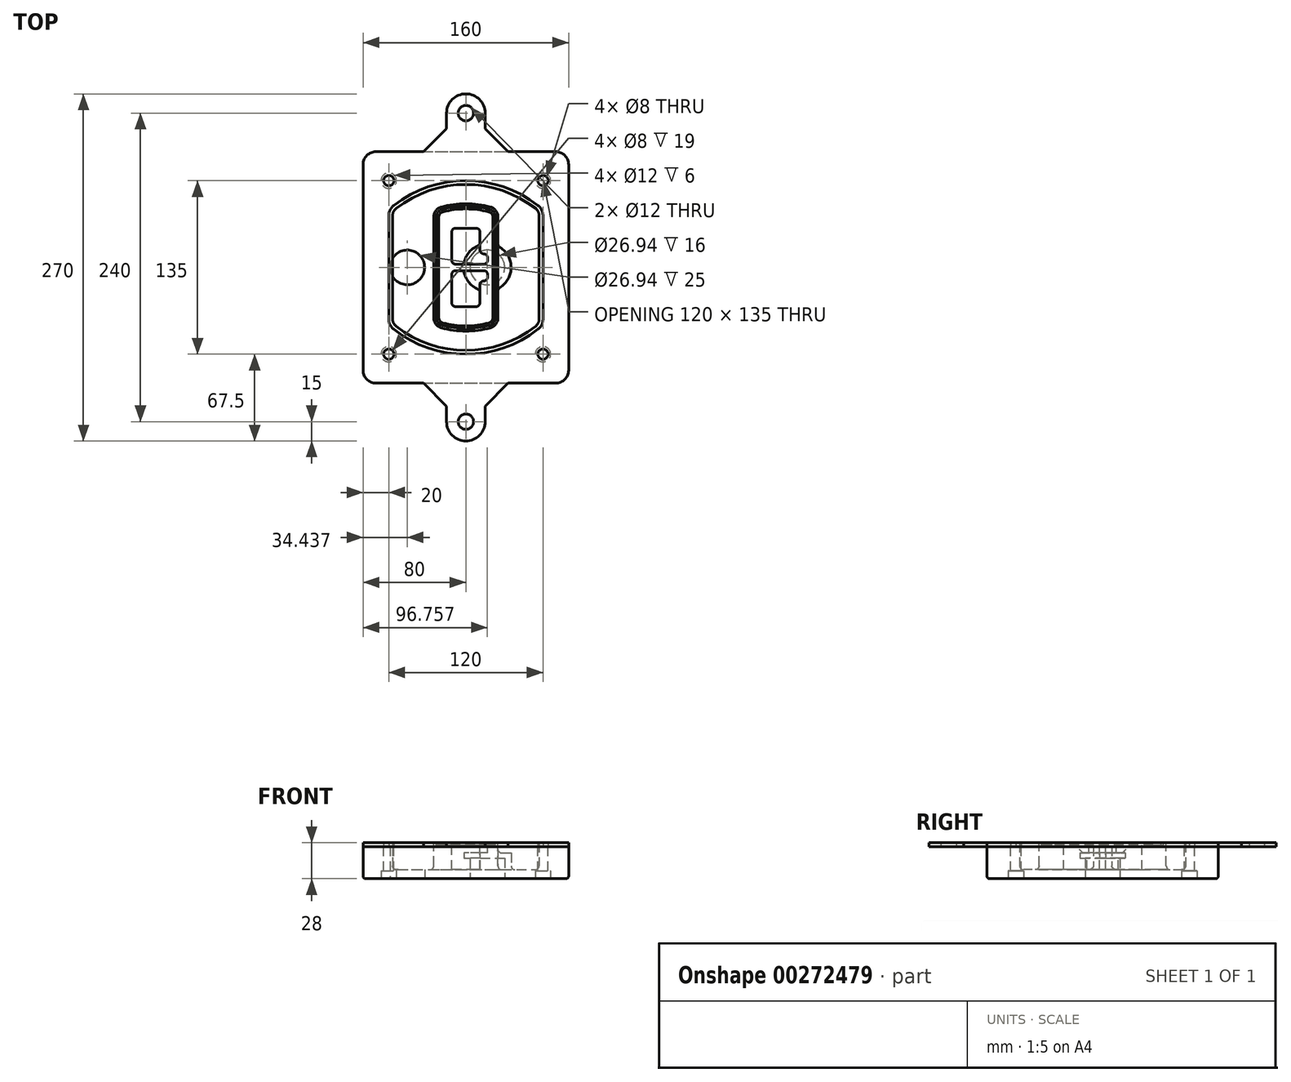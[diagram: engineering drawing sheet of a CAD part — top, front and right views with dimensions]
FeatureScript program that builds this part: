
annotation { "Feature Type Name" : "Feature", "Feature Type Description" : "" }
export const myFeature = defineFeature(function(context is Context, id is Id, definition is map)
    precondition{}
    {
        {
            var Q0;
            Q0=qCreatedBy(makeId("Top.planeOp"),FACE);
            var sketch = newSketch(context, id + "F0", { "sketchPlane" : qUnion([Q0])});
            skPoint(sketch, "E0.rect.middle", {"position": v(0, 0) * mm});
            skLineSegment(sketch, "E1.bottom", {"start": v(-70, -90) * mm, "end": v(70, -90) * mm});
            skLineSegment(sketch, "E1.top", {"start": v(-70, 90) * mm, "end": v(70, 90) * mm});
            skLineSegment(sketch, "E1.left", {"start": v(-80, -80) * mm, "end": v(-80, 80) * mm});
            skLineSegment(sketch, "E1.right", {"start": v(80, -80) * mm, "end": v(80, 80) * mm});
            skLineSegment(sketch, "E2", {"start": v(-80, 90) * mm, "end": v(80, -90) * mm, "construction": true});
            skLineSegment(sketch, "E3", {"start": v(80, 90) * mm, "end": v(-80, -90) * mm, "construction": true});
            skCircle(sketch, "E4", {"center": v(-60, 67.5) * mm, "radius": 4 * mm});
            skCircle(sketch, "E5", {"center": v(60, 67.5) * mm, "radius": 4 * mm});
            skCircle(sketch, "E6", {"center": v(60, -67.5) * mm, "radius": 4 * mm});
            skCircle(sketch, "E7", {"center": v(-60, -67.5) * mm, "radius": 4 * mm});
            skLineSegment(sketch, "E8", {"start": v(-60, 67.5) * mm, "end": v(60, 67.5) * mm, "construction": true});
            skLineSegment(sketch, "E9", {"start": v(60, 67.5) * mm, "end": v(60, -67.5) * mm, "construction": true});
            skLineSegment(sketch, "E10", {"start": v(60, -67.5) * mm, "end": v(-60, -67.5) * mm, "construction": true});
            skLineSegment(sketch, "E11", {"start": v(-60, -67.5) * mm, "end": v(-60, 67.5) * mm, "construction": true});
            skLineSegment(sketch, "E12", {"start": v(-60, 40.3) * mm, "end": v(-60, -40.3) * mm});
            skLineSegment(sketch, "E13", {"start": v(60, 40.3) * mm, "end": v(60, -40.3) * mm});
            skArc(sketch, "E14", {"start": v(56.15, 48.18) * mm, "mid": v(0, 67.5) * mm, "end": v(-56.15, 48.18) * mm});
            skArc(sketch, "E15", {"start": v(-56.15, -48.18) * mm, "mid": v(0, -67.5) * mm, "end": v(56.15, -48.18) * mm});
            skLineSegment(sketch, "E16", {"start": v(-60, 0) * mm, "end": v(60, 0) * mm, "construction": true});
            skPoint(sketch, "E17.visualSharp", {"position": v(-60, -45) * mm});
            skArc(sketch, "E17.filletArc", {"start": v(-60, -40.3) * mm, "mid": v(-58.99, -44.68) * mm, "end": v(-56.15, -48.18) * mm});
            skPoint(sketch, "E18.visualSharp", {"position": v(-60, 45) * mm});
            skArc(sketch, "E18.filletArc", {"start": v(-56.15, 48.18) * mm, "mid": v(-58.99, 44.68) * mm, "end": v(-60, 40.3) * mm});
            skPoint(sketch, "E19.visualSharp", {"position": v(60, 45) * mm});
            skArc(sketch, "E19.filletArc", {"start": v(60, 40.3) * mm, "mid": v(58.99, 44.68) * mm, "end": v(56.15, 48.18) * mm});
            skPoint(sketch, "E20.visualSharp", {"position": v(60, -45) * mm});
            skArc(sketch, "E20.filletArc", {"start": v(56.15, -48.18) * mm, "mid": v(58.99, -44.68) * mm, "end": v(60, -40.3) * mm});
            skPoint(sketch, "E21.visualSharp", {"position": v(-80, 90) * mm});
            skArc(sketch, "E21.filletArc", {"start": v(-70, 90) * mm, "mid": v(-77.07, 87.07) * mm, "end": v(-80, 80) * mm});
            skPoint(sketch, "E22.visualSharp", {"position": v(80, 90) * mm});
            skArc(sketch, "E22.filletArc", {"start": v(80, 80) * mm, "mid": v(77.07, 87.07) * mm, "end": v(70, 90) * mm});
            skPoint(sketch, "E23.visualSharp", {"position": v(80, -90) * mm});
            skArc(sketch, "E23.filletArc", {"start": v(70, -90) * mm, "mid": v(77.07, -87.07) * mm, "end": v(80, -80) * mm});
            skPoint(sketch, "E24.visualSharp", {"position": v(-80, -90) * mm});
            skArc(sketch, "E24.filletArc", {"start": v(-80, -80) * mm, "mid": v(-77.07, -87.07) * mm, "end": v(-70, -90) * mm});
            skArc(sketch, "E25.0", {"start": v(57, 40.3) * mm, "mid": v(56.3, 43.36) * mm, "end": v(54.3, 45.81) * mm});
            skLineSegment(sketch, "E25.1", {"start": v(57, 40.3) * mm, "end": v(57, -40.3) * mm});
            skArc(sketch, "E25.2", {"start": v(54.3, -45.81) * mm, "mid": v(56.3, -43.36) * mm, "end": v(57, -40.3) * mm});
            skArc(sketch, "E25.3", {"start": v(-54.3, -45.81) * mm, "mid": v(0, -64.5) * mm, "end": v(54.3, -45.81) * mm});
            skArc(sketch, "E25.4", {"start": v(-57, -40.3) * mm, "mid": v(-56.3, -43.36) * mm, "end": v(-54.3, -45.81) * mm});
            skArc(sketch, "E25.5", {"start": v(54.3, 45.81) * mm, "mid": v(0, 64.5) * mm, "end": v(-54.3, 45.81) * mm});
            skLineSegment(sketch, "E25.6", {"start": v(-57, 40.3) * mm, "end": v(-57, -40.3) * mm});
            skArc(sketch, "E25.7", {"start": v(-54.3, 45.81) * mm, "mid": v(-56.3, 43.36) * mm, "end": v(-57, 40.3) * mm});
            skArc(sketch, "E26.0", {"start": v(-58.62, 51.33) * mm, "mid": v(-62.58, 46.43) * mm, "end": v(-64, 40.3) * mm});
            skArc(sketch, "E26.1", {"start": v(58.62, 51.33) * mm, "mid": v(0, 71.5) * mm, "end": v(-58.62, 51.33) * mm});
            skArc(sketch, "E26.2", {"start": v(64, 40.3) * mm, "mid": v(62.58, 46.43) * mm, "end": v(58.62, 51.33) * mm});
            skLineSegment(sketch, "E26.3", {"start": v(64, 40.3) * mm, "end": v(64, -40.3) * mm});
            skArc(sketch, "E26.4", {"start": v(58.62, -51.33) * mm, "mid": v(62.58, -46.43) * mm, "end": v(64, -40.3) * mm});
            skLineSegment(sketch, "E26.5", {"start": v(-64, 40.3) * mm, "end": v(-64, -40.3) * mm});
            skArc(sketch, "E26.6", {"start": v(-58.62, -51.33) * mm, "mid": v(0, -71.5) * mm, "end": v(58.62, -51.33) * mm});
            skArc(sketch, "E26.7", {"start": v(-64, -40.3) * mm, "mid": v(-62.58, -46.43) * mm, "end": v(-58.62, -51.33) * mm});
            skSolve(sketch);
        }
        {
            var Q0;
            Q0=makeQuery(id+"F0.imprint","IMPRINT",FACE,{"disambiguationData":[TD([[makeQuery(id+"F0.imprint","IMPRINT",EDGE,{"derivedFrom":sQuery(id+"F0.wireOp",EDGE,"E1.bottom")}),1.0]])]});
            var Q1;
            Q1=makeQuery(id+"F0.imprint","IMPRINT",FACE,{"disambiguationData":[TD([[makeQuery(id+"F0.imprint","IMPRINT",EDGE,{"derivedFrom":sQuery(id+"F0.wireOp",EDGE,"E12")}),1.0]])]});
            var Q2;
            Q2=makeQuery(id+"F0.imprint","IMPRINT",FACE,{"disambiguationData":[TD([[makeQuery(id+"F0.imprint","IMPRINT",EDGE,{"derivedFrom":sQuery(id+"F0.wireOp",EDGE,"E25.0")}),1.0]])]});
            var Q3;
            Q3=makeQuery(id+"F0.imprint","IMPRINT",FACE,{"disambiguationData":[TD([[makeQuery(id+"F0.imprint","IMPRINT",EDGE,{"derivedFrom":sQuery(id+"F0.wireOp",EDGE,"E12")}),-1.0]])]});
            extrude(context, id + "F1", {"entities" : qUnion([Q0, Q1, Q2, Q3]), "oppositeDirection" : true, "depth" : 25 * mm});
        }
        {
            var Q0;
            Q0=makeQuery(id+"F0.imprint","IMPRINT",FACE,{"disambiguationData":[TD([[makeQuery(id+"F0.imprint","IMPRINT",EDGE,{"derivedFrom":sQuery(id+"F0.wireOp",EDGE,"E12")}),1.0]])]});
            extrude(context, id + "F2", {"entities" : qUnion([Q0]), "operationType" : NewBodyOperationType.ADD, "depth" : 3 * mm});
        }
        {
            var Q0;
            Q0=makeQuery(id+"F0.imprint","IMPRINT",FACE,{"disambiguationData":[TD([[makeQuery(id+"F0.imprint","IMPRINT",EDGE,{"derivedFrom":sQuery(id+"F0.wireOp",EDGE,"E25.0")}),1.0]])]});
            extrude(context, id + "F3", {"entities" : qUnion([Q0]), "operationType" : NewBodyOperationType.REMOVE, "oppositeDirection" : true, "depth" : 18 * mm});
        }
        {
            var Q0;
            Q0=makeQuery(id+"F2.opExtrude","CAP_FACE",FACE,{"disambiguationData":[OSD([sQuery(id+"F0.wireOp",EDGE,"E12"),sQuery(id+"F0.wireOp",EDGE,"E13"),sQuery(id+"F0.wireOp",EDGE,"E14"),sQuery(id+"F0.wireOp",EDGE,"E15"),sQuery(id+"F0.wireOp",EDGE,"E17.filletArc"),sQuery(id+"F0.wireOp",EDGE,"E18.filletArc"),sQuery(id+"F0.wireOp",EDGE,"E19.filletArc"),sQuery(id+"F0.wireOp",EDGE,"E20.filletArc"),sQuery(id+"F0.wireOp",EDGE,"E25.0"),sQuery(id+"F0.wireOp",EDGE,"E25.1"),sQuery(id+"F0.wireOp",EDGE,"E25.2"),sQuery(id+"F0.wireOp",EDGE,"E25.3"),sQuery(id+"F0.wireOp",EDGE,"E25.4"),sQuery(id+"F0.wireOp",EDGE,"E25.5"),sQuery(id+"F0.wireOp",EDGE,"E25.6"),sQuery(id+"F0.wireOp",EDGE,"E25.7")])],"isStart":false});
            var sketch = newSketch(context, id + "F4", { "sketchPlane" : qUnion([Q0])});
            skArc(sketch, "E27.0", {"start": v(-19.08, -46.97) * mm, "mid": v(0, -49.5) * mm, "end": v(19.08, -46.97) * mm});
            skArc(sketch, "E28.0", {"start": v(19.08, 46.97) * mm, "mid": v(0, 49.5) * mm, "end": v(-19.08, 46.97) * mm});
            skLineSegment(sketch, "E29", {"start": v(-25, 39.25) * mm, "end": v(-25, -39.25) * mm});
            skLineSegment(sketch, "E30", {"start": v(25, 39.25) * mm, "end": v(25, -39.25) * mm});
            skLineSegment(sketch, "E31", {"start": v(-25, 45.1) * mm, "end": v(25, 45.1) * mm, "construction": true});
            skLineSegment(sketch, "E32", {"start": v(-25, -45.1) * mm, "end": v(25, -45.1) * mm, "construction": true});
            skPoint(sketch, "E33.visualSharp", {"position": v(-25, 45.1) * mm});
            skArc(sketch, "E33.filletArc", {"start": v(-19.08, 46.97) * mm, "mid": v(-23.35, 44.11) * mm, "end": v(-25, 39.25) * mm});
            skPoint(sketch, "E34.visualSharp", {"position": v(25, 45.1) * mm});
            skArc(sketch, "E34.filletArc", {"start": v(25, 39.25) * mm, "mid": v(23.35, 44.11) * mm, "end": v(19.08, 46.97) * mm});
            skPoint(sketch, "E35.visualSharp", {"position": v(25, -45.1) * mm});
            skArc(sketch, "E35.filletArc", {"start": v(19.08, -46.97) * mm, "mid": v(23.35, -44.11) * mm, "end": v(25, -39.25) * mm});
            skPoint(sketch, "E36.visualSharp", {"position": v(-25, -45.1) * mm});
            skArc(sketch, "E36.filletArc", {"start": v(-25, -39.25) * mm, "mid": v(-23.35, -44.11) * mm, "end": v(-19.08, -46.97) * mm});
            skArc(sketch, "E37.0", {"start": v(54.3, 45.81) * mm, "mid": v(0, 64.5) * mm, "end": v(-54.3, 45.81) * mm});
            skArc(sketch, "E37.1", {"start": v(-54.3, 45.81) * mm, "mid": v(-56.3, 43.36) * mm, "end": v(-57, 40.3) * mm});
            skLineSegment(sketch, "E37.2", {"start": v(-57, 40.3) * mm, "end": v(-57, -40.3) * mm});
            skArc(sketch, "E37.3", {"start": v(-57, -40.3) * mm, "mid": v(-56.3, -43.36) * mm, "end": v(-54.3, -45.81) * mm});
            skArc(sketch, "E37.4", {"start": v(-54.3, -45.81) * mm, "mid": v(0, -64.5) * mm, "end": v(54.3, -45.81) * mm});
            skArc(sketch, "E37.5", {"start": v(54.3, -45.81) * mm, "mid": v(56.3, -43.36) * mm, "end": v(57, -40.3) * mm});
            skLineSegment(sketch, "E37.6", {"start": v(57, 40.3) * mm, "end": v(57, -40.3) * mm});
            skArc(sketch, "E37.7", {"start": v(57, 40.3) * mm, "mid": v(56.3, 43.36) * mm, "end": v(54.3, 45.81) * mm});
            skLineSegment(sketch, "E38.0", {"start": v(23, 39.25) * mm, "end": v(23, -39.25) * mm});
            skArc(sketch, "E38.1", {"start": v(18.56, -45.04) * mm, "mid": v(21.76, -42.9) * mm, "end": v(23, -39.25) * mm});
            skArc(sketch, "E38.2", {"start": v(-18.56, -45.04) * mm, "mid": v(0, -47.5) * mm, "end": v(18.56, -45.04) * mm});
            skArc(sketch, "E38.3", {"start": v(-23, -39.25) * mm, "mid": v(-21.76, -42.9) * mm, "end": v(-18.56, -45.04) * mm});
            skLineSegment(sketch, "E38.4", {"start": v(-23, 39.25) * mm, "end": v(-23, -39.25) * mm});
            skArc(sketch, "E38.5", {"start": v(23, 39.25) * mm, "mid": v(21.76, 42.9) * mm, "end": v(18.56, 45.04) * mm});
            skArc(sketch, "E38.6", {"start": v(-18.56, 45.04) * mm, "mid": v(-21.76, 42.9) * mm, "end": v(-23, 39.25) * mm});
            skArc(sketch, "E38.7", {"start": v(18.56, 45.04) * mm, "mid": v(0, 47.5) * mm, "end": v(-18.56, 45.04) * mm});
            skArc(sketch, "E39.0", {"start": v(21, 39.25) * mm, "mid": v(20.18, 41.68) * mm, "end": v(18.04, 43.1) * mm});
            skLineSegment(sketch, "E39.1", {"start": v(21, 39.25) * mm, "end": v(21, -39.25) * mm});
            skArc(sketch, "E39.2", {"start": v(18.04, -43.1) * mm, "mid": v(20.18, -41.68) * mm, "end": v(21, -39.25) * mm});
            skArc(sketch, "E39.3", {"start": v(-18.04, -43.1) * mm, "mid": v(0, -45.5) * mm, "end": v(18.04, -43.1) * mm});
            skArc(sketch, "E39.4", {"start": v(-21, -39.25) * mm, "mid": v(-20.18, -41.68) * mm, "end": v(-18.04, -43.1) * mm});
            skArc(sketch, "E39.5", {"start": v(18.04, 43.1) * mm, "mid": v(0, 45.5) * mm, "end": v(-18.04, 43.1) * mm});
            skLineSegment(sketch, "E39.6", {"start": v(-21, 39.25) * mm, "end": v(-21, -39.25) * mm});
            skArc(sketch, "E39.7", {"start": v(-18.04, 43.1) * mm, "mid": v(-20.18, 41.68) * mm, "end": v(-21, 39.25) * mm});
            skLineSegment(sketch, "E40", {"start": v(-25, 0) * mm, "end": v(25, 0) * mm, "construction": true});
            skLineSegment(sketch, "E41", {"start": v(-11, 5.5) * mm, "end": v(-11, 27.5) * mm});
            skLineSegment(sketch, "E42", {"start": v(-8, 30.5) * mm, "end": v(8, 30.5) * mm});
            skLineSegment(sketch, "E43", {"start": v(11, 27.5) * mm, "end": v(11, 13.5) * mm});
            skLineSegment(sketch, "E44", {"start": v(14, 10.5) * mm, "end": v(14, 10.5) * mm});
            skLineSegment(sketch, "E45", {"start": v(17, 7.5) * mm, "end": v(17, 5.5) * mm});
            skLineSegment(sketch, "E46", {"start": v(14, 2.5) * mm, "end": v(-8, 2.5) * mm});
            skPoint(sketch, "E47.visualSharp", {"position": v(-11, 30.5) * mm});
            skArc(sketch, "E47.filletArc", {"start": v(-8, 30.5) * mm, "mid": v(-10.12, 29.62) * mm, "end": v(-11, 27.5) * mm});
            skPoint(sketch, "E48.visualSharp", {"position": v(11, 30.5) * mm});
            skArc(sketch, "E48.filletArc", {"start": v(11, 27.5) * mm, "mid": v(10.12, 29.62) * mm, "end": v(8, 30.5) * mm});
            skPoint(sketch, "E49.visualSharp", {"position": v(11, 10.5) * mm});
            skArc(sketch, "E49.filletArc", {"start": v(11, 13.5) * mm, "mid": v(11.88, 11.38) * mm, "end": v(14, 10.5) * mm});
            skPoint(sketch, "E50.visualSharp", {"position": v(17, 10.5) * mm});
            skArc(sketch, "E50.filletArc", {"start": v(17, 7.5) * mm, "mid": v(16.12, 9.62) * mm, "end": v(14, 10.5) * mm});
            skPoint(sketch, "E51.visualSharp", {"position": v(17, 2.5) * mm});
            skArc(sketch, "E51.filletArc", {"start": v(14, 2.5) * mm, "mid": v(16.12, 3.38) * mm, "end": v(17, 5.5) * mm});
            skPoint(sketch, "E52.visualSharp", {"position": v(-11, 2.5) * mm});
            skArc(sketch, "E52.filletArc", {"start": v(-11, 5.5) * mm, "mid": v(-10.12, 3.38) * mm, "end": v(-8, 2.5) * mm});
            skLineSegment(sketch, "E53.0.MirrorCS", {"start": v(14, -2.5) * mm, "end": v(-8, -2.5) * mm});
            skArc(sketch, "E54.0.MirrorCS", {"start": v(-11, -5.5) * mm, "mid": v(-10.12, -3.38) * mm, "end": v(-8, -2.5) * mm});
            skLineSegment(sketch, "E55.0.MirrorCS", {"start": v(-11, -5.5) * mm, "end": v(-11, -27.5) * mm});
            skArc(sketch, "E56.0.MirrorCS", {"start": v(-8, -30.5) * mm, "mid": v(-10.12, -29.62) * mm, "end": v(-11, -27.5) * mm});
            skLineSegment(sketch, "E57.0.MirrorCS", {"start": v(-8, -30.5) * mm, "end": v(8, -30.5) * mm});
            skArc(sketch, "E58.0.MirrorCS", {"start": v(11, -27.5) * mm, "mid": v(10.12, -29.62) * mm, "end": v(8, -30.5) * mm});
            skLineSegment(sketch, "E59.0.MirrorCS", {"start": v(11, -27.5) * mm, "end": v(11, -13.5) * mm});
            skArc(sketch, "E60.0.MirrorCS", {"start": v(11, -13.5) * mm, "mid": v(11.88, -11.38) * mm, "end": v(14, -10.5) * mm});
            skArc(sketch, "E61.0.MirrorCS", {"start": v(17, -7.5) * mm, "mid": v(16.12, -9.62) * mm, "end": v(14, -10.5) * mm});
            skLineSegment(sketch, "E62.0.MirrorCS", {"start": v(17, -7.5) * mm, "end": v(17, -5.5) * mm});
            skArc(sketch, "E63.0.MirrorCS", {"start": v(14, -2.5) * mm, "mid": v(16.12, -3.38) * mm, "end": v(17, -5.5) * mm});
            skSolve(sketch);
        }
        {
            var Q0;
            Q0=makeQuery(id+"F4.imprint","IMPRINT",FACE,{"disambiguationData":[TD([[makeQuery(id+"F4.imprint","IMPRINT",EDGE,{"derivedFrom":sQuery(id+"F4.wireOp",EDGE,"E27.0")}),1.0]])]});
            var Q1;
            Q1=makeQuery(id+"F4.imprint","IMPRINT",FACE,{"disambiguationData":[TD([[makeQuery(id+"F4.imprint","IMPRINT",EDGE,{"derivedFrom":sQuery(id+"F4.wireOp",EDGE,"E38.0")}),-1.0]])]});
            var Q2;
            Q2=makeQuery(id+"F4.imprint","IMPRINT",FACE,{"disambiguationData":[TD([[makeQuery(id+"F4.imprint","IMPRINT",EDGE,{"derivedFrom":sQuery(id+"F4.wireOp",EDGE,"E39.0")}),1.0]])]});
            extrude(context, id + "F5", {"entities" : qUnion([Q0, Q1, Q2]), "operationType" : NewBodyOperationType.ADD, "endBound" : BoundingType.UP_TO_NEXT, "oppositeDirection" : true, "depth" : 25 * mm});
        }
        {
            var Q0;
            Q0=makeQuery(id+"F4.imprint","IMPRINT",FACE,{"disambiguationData":[TD([[makeQuery(id+"F4.imprint","IMPRINT",EDGE,{"derivedFrom":sQuery(id+"F4.wireOp",EDGE,"E38.0")}),-1.0]])]});
            extrude(context, id + "F6", {"entities" : qUnion([Q0]), "operationType" : NewBodyOperationType.REMOVE, "oppositeDirection" : true, "depth" : 2 * mm});
        }
        {
            var Q0;
            Q0=makeQuery(id+"F1.opExtrude","CAP_FACE",FACE,{"disambiguationData":[OSD([sQuery(id+"F0.wireOp",EDGE,"E1.bottom"),sQuery(id+"F0.wireOp",EDGE,"E1.top"),sQuery(id+"F0.wireOp",EDGE,"E1.left"),sQuery(id+"F0.wireOp",EDGE,"E1.right"),sQuery(id+"F0.wireOp",EDGE,"E4"),sQuery(id+"F0.wireOp",EDGE,"E5"),sQuery(id+"F0.wireOp",EDGE,"E6"),sQuery(id+"F0.wireOp",EDGE,"E7"),sQuery(id+"F0.wireOp",EDGE,"E21.filletArc"),sQuery(id+"F0.wireOp",EDGE,"E22.filletArc"),sQuery(id+"F0.wireOp",EDGE,"E23.filletArc"),sQuery(id+"F0.wireOp",EDGE,"E24.filletArc")])],"isStart":false});
            var sketch = newSketch(context, id + "F7", { "sketchPlane" : qUnion([Q0])});
            skCircle(sketch, "E64", {"center": v(16.76, 0) * mm, "radius": 13.47 * mm});
            skCircle(sketch, "E65", {"center": v(-45.56, 0) * mm, "radius": 13.47 * mm});
            skLineSegment(sketch, "E66", {"start": v(80, 0) * mm, "end": v(-80, 0) * mm});
            skCircle(sketch, "E67", {"center": v(16.76, 0) * mm, "radius": 18.47 * mm});
            skCircle(sketch, "E68", {"center": v(60, -67.5) * mm, "radius": 6 * mm});
            skCircle(sketch, "E69", {"center": v(-60, -67.5) * mm, "radius": 6 * mm});
            skCircle(sketch, "E70", {"center": v(-60, 67.5) * mm, "radius": 6 * mm});
            skCircle(sketch, "E71", {"center": v(60, 67.5) * mm, "radius": 6 * mm});
            skSolve(sketch);
        }
        {
            var Q0;
            {var subQ1=sQuery(id+"F7.wireOp",EDGE,"E66");var subQ4=sQuery(id+"F7.wireOp",EDGE,"E64");var subQ6=makeQuery(id+"F7.imprint","INTERSECT",VERTEX,{"disambiguationData":[OD(0.0)],"derivedFrom":[subQ4,subQ1]});Q0=makeQuery(id+"F7.imprint","IMPRINT",FACE,{"disambiguationData":[TD([[makeQuery(id+"F7.imprint","IMPRINT",EDGE,{"disambiguationData":[TD([[subQ6,-1.0]])],"derivedFrom":subQ4}),-1.0]])]});}
            var Q1;
            {var subQ0=sQuery(id+"F7.wireOp",EDGE,"E66");var subQ1=sQuery(id+"F7.wireOp",EDGE,"E64");var subQ3=makeQuery(id+"F7.imprint","INTERSECT",VERTEX,{"disambiguationData":[OD(0.0)],"derivedFrom":[subQ1,subQ0]});Q1=makeQuery(id+"F7.imprint","IMPRINT",FACE,{"disambiguationData":[TD([[makeQuery(id+"F7.imprint","IMPRINT",EDGE,{"disambiguationData":[TD([[subQ3,-1.0]])],"derivedFrom":subQ1}),1.0]])]});}
            var Q2;
            {var subQ0=sQuery(id+"F7.wireOp",EDGE,"E66");var subQ1=sQuery(id+"F7.wireOp",EDGE,"E64");var subQ3=makeQuery(id+"F7.imprint","INTERSECT",VERTEX,{"disambiguationData":[OD(0.0)],"derivedFrom":[subQ1,subQ0]});Q2=makeQuery(id+"F7.imprint","IMPRINT",FACE,{"disambiguationData":[TD([[makeQuery(id+"F7.imprint","IMPRINT",EDGE,{"disambiguationData":[TD([[subQ3,1.0]])],"derivedFrom":subQ1}),1.0]])]});}
            var Q3;
            {var subQ1=sQuery(id+"F7.wireOp",EDGE,"E66");var subQ4=sQuery(id+"F7.wireOp",EDGE,"E64");var subQ6=makeQuery(id+"F7.imprint","INTERSECT",VERTEX,{"disambiguationData":[OD(0.0)],"derivedFrom":[subQ4,subQ1]});Q3=makeQuery(id+"F7.imprint","IMPRINT",FACE,{"disambiguationData":[TD([[makeQuery(id+"F7.imprint","IMPRINT",EDGE,{"disambiguationData":[TD([[subQ6,1.0]])],"derivedFrom":subQ4}),-1.0]])]});}
            extrude(context, id + "F8", {"entities" : qUnion([Q0, Q1, Q2, Q3]), "operationType" : NewBodyOperationType.ADD, "oppositeDirection" : true, "depth" : 20 * mm});
        }
        {
            var Q0;
            {var subQ0=sQuery(id+"F7.wireOp",EDGE,"E66");var subQ1=sQuery(id+"F7.wireOp",EDGE,"E64");var subQ3=makeQuery(id+"F7.imprint","INTERSECT",VERTEX,{"disambiguationData":[OD(0.0)],"derivedFrom":[subQ1,subQ0]});Q0=makeQuery(id+"F7.imprint","IMPRINT",FACE,{"disambiguationData":[TD([[makeQuery(id+"F7.imprint","IMPRINT",EDGE,{"disambiguationData":[TD([[subQ3,-1.0]])],"derivedFrom":subQ1}),1.0]])]});}
            var Q1;
            {var subQ0=sQuery(id+"F7.wireOp",EDGE,"E66");var subQ1=sQuery(id+"F7.wireOp",EDGE,"E64");var subQ3=makeQuery(id+"F7.imprint","INTERSECT",VERTEX,{"disambiguationData":[OD(0.0)],"derivedFrom":[subQ1,subQ0]});Q1=makeQuery(id+"F7.imprint","IMPRINT",FACE,{"disambiguationData":[TD([[makeQuery(id+"F7.imprint","IMPRINT",EDGE,{"disambiguationData":[TD([[subQ3,1.0]])],"derivedFrom":subQ1}),1.0]])]});}
            extrude(context, id + "F9", {"entities" : qUnion([Q0, Q1]), "operationType" : NewBodyOperationType.REMOVE, "oppositeDirection" : true, "depth" : 16 * mm});
        }
        {
            var Q0;
            {var subQ0=sQuery(id+"F7.wireOp",EDGE,"E66");var subQ1=sQuery(id+"F7.wireOp",EDGE,"E65");var subQ3=makeQuery(id+"F7.imprint","INTERSECT",VERTEX,{"disambiguationData":[OD(0.0)],"derivedFrom":[subQ1,subQ0]});Q0=makeQuery(id+"F7.imprint","IMPRINT",FACE,{"disambiguationData":[TD([[makeQuery(id+"F7.imprint","IMPRINT",EDGE,{"disambiguationData":[TD([[subQ3,-1.0]])],"derivedFrom":subQ1}),1.0]])]});}
            var Q1;
            {var subQ0=sQuery(id+"F7.wireOp",EDGE,"E66");var subQ1=sQuery(id+"F7.wireOp",EDGE,"E65");var subQ3=makeQuery(id+"F7.imprint","INTERSECT",VERTEX,{"disambiguationData":[OD(0.0)],"derivedFrom":[subQ1,subQ0]});Q1=makeQuery(id+"F7.imprint","IMPRINT",FACE,{"disambiguationData":[TD([[makeQuery(id+"F7.imprint","IMPRINT",EDGE,{"disambiguationData":[TD([[subQ3,1.0]])],"derivedFrom":subQ1}),1.0]])]});}
            extrude(context, id + "F10", {"entities" : qUnion([Q0, Q1]), "operationType" : NewBodyOperationType.REMOVE, "oppositeDirection" : true, "depth" : 25 * mm});
        }
        {
            var Q0;
            Q0=makeQuery(id+"F7.imprint","IMPRINT",FACE,{"disambiguationData":[TD([[makeQuery(id+"F7.imprint","IMPRINT",EDGE,{"derivedFrom":sQuery(id+"F7.wireOp",EDGE,"E68")}),1.0]])]});
            var Q1;
            Q1=makeQuery(id+"F7.imprint","IMPRINT",FACE,{"disambiguationData":[TD([[makeQuery(id+"F7.imprint","IMPRINT",EDGE,{"derivedFrom":makeQuery(id+"F1.opExtrude","CAP_EDGE",EDGE,{"disambiguationData":[OSD([sQuery(id+"F0.wireOp",EDGE,"E5")])],"isStart":false})}),-1.0]])]});
            var Q2;
            Q2=makeQuery(id+"F7.imprint","IMPRINT",FACE,{"disambiguationData":[TD([[makeQuery(id+"F7.imprint","IMPRINT",EDGE,{"derivedFrom":sQuery(id+"F7.wireOp",EDGE,"E69")}),1.0]])]});
            var Q3;
            Q3=makeQuery(id+"F7.imprint","IMPRINT",FACE,{"disambiguationData":[TD([[makeQuery(id+"F7.imprint","IMPRINT",EDGE,{"derivedFrom":makeQuery(id+"F1.opExtrude","CAP_EDGE",EDGE,{"disambiguationData":[OSD([sQuery(id+"F0.wireOp",EDGE,"E4")])],"isStart":false})}),-1.0]])]});
            var Q4;
            Q4=makeQuery(id+"F7.imprint","IMPRINT",FACE,{"disambiguationData":[TD([[makeQuery(id+"F7.imprint","IMPRINT",EDGE,{"derivedFrom":sQuery(id+"F7.wireOp",EDGE,"E70")}),1.0]])]});
            var Q5;
            Q5=makeQuery(id+"F7.imprint","IMPRINT",FACE,{"disambiguationData":[TD([[makeQuery(id+"F7.imprint","IMPRINT",EDGE,{"derivedFrom":makeQuery(id+"F1.opExtrude","CAP_EDGE",EDGE,{"disambiguationData":[OSD([sQuery(id+"F0.wireOp",EDGE,"E7")])],"isStart":false})}),-1.0]])]});
            var Q6;
            Q6=makeQuery(id+"F7.imprint","IMPRINT",FACE,{"disambiguationData":[TD([[makeQuery(id+"F7.imprint","IMPRINT",EDGE,{"derivedFrom":sQuery(id+"F7.wireOp",EDGE,"E71")}),1.0]])]});
            var Q7;
            Q7=makeQuery(id+"F7.imprint","IMPRINT",FACE,{"disambiguationData":[TD([[makeQuery(id+"F7.imprint","IMPRINT",EDGE,{"derivedFrom":makeQuery(id+"F1.opExtrude","CAP_EDGE",EDGE,{"disambiguationData":[OSD([sQuery(id+"F0.wireOp",EDGE,"E6")])],"isStart":false})}),-1.0]])]});
            extrude(context, id + "F11", {"entities" : qUnion([Q0, Q1, Q2, Q3, Q4, Q5, Q6, Q7]), "operationType" : NewBodyOperationType.REMOVE, "oppositeDirection" : true, "depth" : 6 * mm});
        }
        {
            var Q0;
            Q0=makeQuery(id+"F9.boolean.opBoolean","COPY",FACE,{"derivedFrom":makeQuery(id+"F9.opExtrude","CAP_FACE",FACE,{"disambiguationData":[OSD([sQuery(id+"F7.wireOp",EDGE,"E64")])],"isStart":false})});
            var sketch = newSketch(context, id + "F12", { "sketchPlane" : qUnion([Q0])});
            skArc(sketch, "E72.0", {"start": v(11, 17.55) * mm, "mid": v(2.57, 11.82) * mm, "end": v(-1.54, 2.5) * mm});
            skArc(sketch, "E72.1", {"start": v(-1.54, -2.5) * mm, "mid": v(2.57, -11.82) * mm, "end": v(11, -17.55) * mm});
            skLineSegment(sketch, "E73", {"start": v(-1.54, -2.5) * mm, "end": v(14, -2.5) * mm});
            skLineSegment(sketch, "E74.0", {"start": v(14, 2.5) * mm, "end": v(-1.54, 2.5) * mm});
            skArc(sketch, "E74.1", {"start": v(14, 2.5) * mm, "mid": v(16.12, 3.38) * mm, "end": v(17, 5.5) * mm});
            skLineSegment(sketch, "E74.2", {"start": v(17, 7.5) * mm, "end": v(17, 5.5) * mm});
            skArc(sketch, "E74.3", {"start": v(17, 7.5) * mm, "mid": v(16.12, 9.62) * mm, "end": v(14, 10.5) * mm});
            skArc(sketch, "E74.4", {"start": v(11, 13.5) * mm, "mid": v(11.88, 11.38) * mm, "end": v(14, 10.5) * mm});
            skLineSegment(sketch, "E74.5", {"start": v(11, 17.55) * mm, "end": v(11, 13.5) * mm});
            skLineSegment(sketch, "E74.7", {"start": v(14, -2.5) * mm, "end": v(-1.54, -2.5) * mm});
            skArc(sketch, "E74.8", {"start": v(14, -2.5) * mm, "mid": v(16.12, -3.38) * mm, "end": v(17, -5.5) * mm});
            skLineSegment(sketch, "E74.9", {"start": v(17, -7.5) * mm, "end": v(17, -5.5) * mm});
            skArc(sketch, "E74.10", {"start": v(17, -7.5) * mm, "mid": v(16.12, -9.62) * mm, "end": v(14, -10.5) * mm});
            skArc(sketch, "E74.11", {"start": v(11, -13.5) * mm, "mid": v(11.88, -11.38) * mm, "end": v(14, -10.5) * mm});
            skLineSegment(sketch, "E74.12", {"start": v(11, -17.55) * mm, "end": v(11, -13.5) * mm});
            skPoint(sketch, "E75.orphan", {"position": v(11, -27.5) * mm});
            skPoint(sketch, "E76.orphan", {"position": v(-8, -2.5) * mm});
            skPoint(sketch, "E77.orphan", {"position": v(-8, 2.5) * mm});
            skPoint(sketch, "E78.orphan", {"position": v(11, 27.5) * mm});
            skSolve(sketch);
        }
        {
            var Q0;
            {var subQ7=sQuery(id+"F12.wireOp",EDGE,"E72.0");var subQ14=sQuery(id+"F12.wireOp",EDGE,"E72.1");var subQ16=sQuery(id+"F12.wireOp",EDGE,"E74.1");var subQ18=sQuery(id+"F12.wireOp",EDGE,"E74.8");Q0=qUnion([makeQuery(id+"F12.imprint","IMPRINT",FACE,{"disambiguationData":[TD([[makeQuery(id+"F12.imprint","IMPRINT",EDGE,{"derivedFrom":subQ7}),1.0]])]}),makeQuery(id+"F12.imprint","IMPRINT",FACE,{"disambiguationData":[TD([[makeQuery(id+"F12.imprint","IMPRINT",EDGE,{"derivedFrom":subQ14}),1.0]])]}),makeQuery(id+"F12.imprint","IMPRINT",FACE,{"disambiguationData":[TD([[makeQuery(id+"F12.imprint","IMPRINT",EDGE,{"derivedFrom":subQ16}),1.0]])]}),makeQuery(id+"F12.imprint","IMPRINT",FACE,{"disambiguationData":[TD([[makeQuery(id+"F12.imprint","IMPRINT",EDGE,{"derivedFrom":subQ18}),-1.0]])]})]);}
            var Q1;
            Q1=makeQuery(id+"F5.boolean.opBoolean","SPLIT",FACE,{"disambiguationData":[TD([makeQuery(id+"F5.opExtrude","SWEPT_FACE",FACE,{"disambiguationData":[OSD([sQuery(id+"F4.wireOp",EDGE,"E41")])]})])],"derivedFrom":makeQuery(id+"F3.boolean.opBoolean","COPY",FACE,{"derivedFrom":makeQuery(id+"F3.opExtrude","CAP_FACE",FACE,{"disambiguationData":[OSD([sQuery(id+"F0.wireOp",EDGE,"E25.0"),sQuery(id+"F0.wireOp",EDGE,"E25.1"),sQuery(id+"F0.wireOp",EDGE,"E25.2"),sQuery(id+"F0.wireOp",EDGE,"E25.3"),sQuery(id+"F0.wireOp",EDGE,"E25.4"),sQuery(id+"F0.wireOp",EDGE,"E25.5"),sQuery(id+"F0.wireOp",EDGE,"E25.6"),sQuery(id+"F0.wireOp",EDGE,"E25.7")])],"isStart":false})})});
            extrude(context, id + "F13", {"entities" : qUnion([Q0]), "operationType" : NewBodyOperationType.REMOVE, "endBound" : BoundingType.UP_TO_SURFACE, "endBoundEntityFace" : qUnion([Q1]), "depth" : 25 * mm});
        }
        {
            var Q0;
            Q0=makeQuery(id+"F3.boolean.opBoolean","COPY",EDGE,{"derivedFrom":makeQuery(id+"F3.opExtrude","CAP_EDGE",EDGE,{"disambiguationData":[OSD([sQuery(id+"F0.wireOp",EDGE,"E25.6")])],"isStart":false})});
            var Q1;
            Q1=makeQuery(id+"F8.boolean.opBoolean","INTERSECT",EDGE,{"derivedFrom":[makeQuery(id+"F5.opExtrude","SWEPT_FACE",FACE,{"disambiguationData":[OSD([sQuery(id+"F4.wireOp",EDGE,"E30")])]}),makeQuery(id+"F8.opExtrude","CAP_FACE",FACE,{"disambiguationData":[OSD([sQuery(id+"F7.wireOp",EDGE,"E67")])],"isStart":false})]});
            var Q2;
            Q2=makeQuery(id+"F8.boolean.opBoolean","INTERSECT",EDGE,{"disambiguationData":[OD(1.0)],"derivedFrom":[makeQuery(id+"F5.opExtrude","SWEPT_FACE",FACE,{"disambiguationData":[OSD([sQuery(id+"F4.wireOp",EDGE,"E30")])]}),makeQuery(id+"F8.opExtrude","SWEPT_FACE",FACE,{"disambiguationData":[OSD([sQuery(id+"F7.wireOp",EDGE,"E67")])]})]});
            var Q3;
            {var subQ0=sQuery(id+"F4.wireOp",EDGE,"E30");Q3=makeQuery(id+"F8.boolean.opBoolean","SPLIT",EDGE,{"disambiguationData":[TD([makeQuery(id+"F5.opExtrude","SWEPT_FACE",FACE,{"disambiguationData":[OSD([sQuery(id+"F4.wireOp",EDGE,"E35.filletArc")])]})])],"derivedFrom":makeQuery(id+"F5.opExtrude","CAP_EDGE",EDGE,{"disambiguationData":[OSD([subQ0])],"isStart":false})});}
            var Q4;
            {var subQ0=sQuery(id+"F0.wireOp",EDGE,"E25.7");var subQ1=sQuery(id+"F0.wireOp",EDGE,"E25.1");var subQ2=sQuery(id+"F0.wireOp",EDGE,"E25.6");var subQ3=sQuery(id+"F0.wireOp",EDGE,"E25.5");var subQ4=sQuery(id+"F0.wireOp",EDGE,"E25.4");var subQ5=sQuery(id+"F0.wireOp",EDGE,"E25.0");var subQ6=sQuery(id+"F0.wireOp",EDGE,"E25.2");var subQ7=sQuery(id+"F0.wireOp",EDGE,"E25.3");Q4=makeQuery(id+"F8.boolean.opBoolean","INTERSECT",EDGE,{"derivedFrom":[makeQuery(id+"F5.boolean.opBoolean","SPLIT",FACE,{"disambiguationData":[TD([makeQuery(id+"F2.opExtrude","SWEPT_FACE",FACE,{"disambiguationData":[OSD([subQ5])]})])],"derivedFrom":makeQuery(id+"F3.boolean.opBoolean","COPY",FACE,{"derivedFrom":makeQuery(id+"F3.opExtrude","CAP_FACE",FACE,{"disambiguationData":[OSD([subQ5,subQ1,subQ6,subQ7,subQ4,subQ3,subQ2,subQ0])],"isStart":false})})}),makeQuery(id+"F8.opExtrude","SWEPT_FACE",FACE,{"disambiguationData":[OSD([sQuery(id+"F7.wireOp",EDGE,"E67")])]})]});}
            var Q5;
            Q5=makeQuery(id+"F8.boolean.opBoolean","INTERSECT",EDGE,{"disambiguationData":[OD(0.0)],"derivedFrom":[makeQuery(id+"F5.opExtrude","SWEPT_FACE",FACE,{"disambiguationData":[OSD([sQuery(id+"F4.wireOp",EDGE,"E30")])]}),makeQuery(id+"F8.opExtrude","SWEPT_FACE",FACE,{"disambiguationData":[OSD([sQuery(id+"F7.wireOp",EDGE,"E67")])]})]});
            fillet(context, id + "F14", {"entities" : qUnion([Q0, Q1, Q2, Q3, Q4, Q5]), "radius" : 3 * mm, "tangentPropagation" : true, "allowEdgeOverflow" : false});
        }
        {
            var Q0;
            Q0=makeQuery(id+"F1.opExtrude","CAP_EDGE",EDGE,{"disambiguationData":[OSD([sQuery(id+"F0.wireOp",EDGE,"E1.bottom")])],"isStart":false});
            fillet(context, id + "F15", {"entities" : qUnion([Q0]), "radius" : 2 * mm, "tangentPropagation" : true, "allowEdgeOverflow" : false});
        }
        {
            var Q0;
            {var subQ0=sQuery(id+"F0.wireOp",EDGE,"E22.filletArc");var subQ1=sQuery(id+"F0.wireOp",EDGE,"E7");var subQ2=sQuery(id+"F0.wireOp",EDGE,"E6");var subQ3=sQuery(id+"F0.wireOp",EDGE,"E5");var subQ4=sQuery(id+"F0.wireOp",EDGE,"E4");var subQ5=sQuery(id+"F0.wireOp",EDGE,"E1.bottom");var subQ6=sQuery(id+"F0.wireOp",EDGE,"E21.filletArc");var subQ7=sQuery(id+"F0.wireOp",EDGE,"E1.top");var subQ8=sQuery(id+"F0.wireOp",EDGE,"E1.left");var subQ9=sQuery(id+"F0.wireOp",EDGE,"E1.right");var subQ10=sQuery(id+"F0.wireOp",EDGE,"E23.filletArc");var subQ11=sQuery(id+"F0.wireOp",EDGE,"E24.filletArc");Q0=makeQuery(id+"F2.boolean.opBoolean","SPLIT",FACE,{"disambiguationData":[TD([makeQuery(id+"F1.opExtrude","SWEPT_FACE",FACE,{"disambiguationData":[OSD([subQ5])]})])],"derivedFrom":makeQuery(id+"F1.opExtrude","CAP_FACE",FACE,{"disambiguationData":[OSD([subQ5,subQ7,subQ8,subQ9,subQ4,subQ3,subQ2,subQ1,subQ6,subQ0,subQ10,subQ11])],"isStart":true})});}
            var sketch = newSketch(context, id + "F16", { "sketchPlane" : qUnion([Q0])});
            skLineSegment(sketch, "E79", {"start": v(0, 90) * mm, "end": v(0, 120) * mm, "construction": true});
            skPoint(sketch, "E79.endSnap0", {"position": v(0, 90) * mm});
            skCircle(sketch, "E80", {"center": v(0, 120) * mm, "radius": 6 * mm});
            skArc(sketch, "E81", {"start": v(15, 120) * mm, "mid": v(0, 135) * mm, "end": v(-15, 120) * mm});
            skLineSegment(sketch, "E82", {"start": v(32.97, 90) * mm, "end": v(15, 108) * mm});
            skLineSegment(sketch, "E83", {"start": v(15, 108) * mm, "end": v(15, 120) * mm});
            skLineSegment(sketch, "E84.MirrorCS", {"start": v(-15, 108) * mm, "end": v(-15, 120) * mm});
            skLineSegment(sketch, "E85.MirrorCS", {"start": v(-32.97, 90) * mm, "end": v(-15, 108) * mm});
            skLineSegment(sketch, "E86", {"start": v(-80, 0) * mm, "end": v(80, 0) * mm, "construction": true});
            skArc(sketch, "E87.MirrorCS", {"start": v(-15, 120) * mm, "mid": v(0, 135) * mm, "end": v(15, 120) * mm});
            skLineSegment(sketch, "E88.MirrorCS", {"start": v(80, 0) * mm, "end": v(-80, 0) * mm, "construction": true});
            skLineSegment(sketch, "E89.MirrorCS", {"start": v(-32.97, -90) * mm, "end": v(-15, -108) * mm});
            skArc(sketch, "E90.MirrorCS", {"start": v(-15, -120) * mm, "mid": v(0, -135) * mm, "end": v(15, -120) * mm});
            skLineSegment(sketch, "E91.MirrorCS", {"start": v(-15, -108) * mm, "end": v(-15, -120) * mm});
            skLineSegment(sketch, "E92.MirrorCS", {"start": v(15, -108) * mm, "end": v(15, -120) * mm});
            skCircle(sketch, "E93.MirrorC", {"center": v(0, -120) * mm, "radius": 6 * mm});
            skLineSegment(sketch, "E94.MirrorCS", {"start": v(32.97, -90) * mm, "end": v(15, -108) * mm});
            skLineSegment(sketch, "E95.MirrorCS", {"start": v(0, -90) * mm, "end": v(0, -120) * mm, "construction": true});
            skArc(sketch, "E96.MirrorCS", {"start": v(15, -120) * mm, "mid": v(0, -135) * mm, "end": v(-15, -120) * mm});
            skSolve(sketch);
        }
        {
            var Q0;
            Q0=makeQuery(id+"F16.imprint","IMPRINT",FACE,{"disambiguationData":[TD([[makeQuery(id+"F16.imprint","IMPRINT",EDGE,{"derivedFrom":sQuery(id+"F16.wireOp",EDGE,"E93.MirrorC")}),-1.0]])]});
            var Q1;
            Q1=makeQuery(id+"F16.imprint","IMPRINT",FACE,{"disambiguationData":[TD([[makeQuery(id+"F16.imprint","IMPRINT",EDGE,{"derivedFrom":makeQuery(id+"F1.opExtrude","CAP_EDGE",EDGE,{"disambiguationData":[OSD([sQuery(id+"F0.wireOp",EDGE,"E1.left")])],"isStart":true})}),-1.0]])]});
            var Q2;
            Q2=makeQuery(id+"F16.imprint","IMPRINT",FACE,{"disambiguationData":[TD([[makeQuery(id+"F16.imprint","IMPRINT",EDGE,{"derivedFrom":sQuery(id+"F16.wireOp",EDGE,"E83")}),1.0]])]});
            var Q3;
            Q3=makeQuery(id+"F2.opExtrude","CAP_FACE",FACE,{"disambiguationData":[OSD([sQuery(id+"F0.wireOp",EDGE,"E12"),sQuery(id+"F0.wireOp",EDGE,"E13"),sQuery(id+"F0.wireOp",EDGE,"E14"),sQuery(id+"F0.wireOp",EDGE,"E15"),sQuery(id+"F0.wireOp",EDGE,"E17.filletArc"),sQuery(id+"F0.wireOp",EDGE,"E18.filletArc"),sQuery(id+"F0.wireOp",EDGE,"E19.filletArc"),sQuery(id+"F0.wireOp",EDGE,"E20.filletArc"),sQuery(id+"F0.wireOp",EDGE,"E25.0"),sQuery(id+"F0.wireOp",EDGE,"E25.1"),sQuery(id+"F0.wireOp",EDGE,"E25.2"),sQuery(id+"F0.wireOp",EDGE,"E25.3"),sQuery(id+"F0.wireOp",EDGE,"E25.4"),sQuery(id+"F0.wireOp",EDGE,"E25.5"),sQuery(id+"F0.wireOp",EDGE,"E25.6"),sQuery(id+"F0.wireOp",EDGE,"E25.7")])],"isStart":false});
            extrude(context, id + "F17", {"entities" : qUnion([Q0, Q1, Q2]), "endBound" : BoundingType.UP_TO_SURFACE, "endBoundEntityFace" : qUnion([Q3]), "depth" : 25 * mm});
        }
    });
